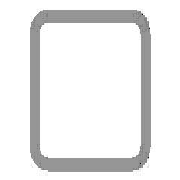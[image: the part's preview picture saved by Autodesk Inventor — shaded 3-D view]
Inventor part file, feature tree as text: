
AUTODESK INVENTOR PART (.ipt)
format: ipt  version: 2024.3 (Build 283343000, 343)  size: 148,480 bytes
history: native  units: mm (DEFAULTED — no unit token found)
features: other x4, plane x3, split x2, sketch x1
ambient origin geometry x8: Origin, YZ Plane, XZ Plane, XY Plane, X Axis, Y Axis, Z Axis, Center Point
bodies: Solid1 (feature_tree), Body (feature_tree)
feature tree (10):
  parser-record x1  (decoder bookkeeping rows leaked as tree rows — omitted from the tree; the rows remain in map.json)
  other  "Driven Length"
  other  "Start Plane"
  other  "End Plane"
  plane  "Work Plane4"
  split  "Split1"
  plane  "Work Plane5"
  split  "Split2"
  sketch  "Sketch3"  dims[d3=270.0mm d4=0.0mm d7=4.0mm d9=20.0mm d11=20.0mm d12=2.0mm d13=-10.0mm d14=260.0mm d15=10.0mm d16=10.0mm d17=90.0deg d18=270.0mm]
  plane  "Work Plane3"
